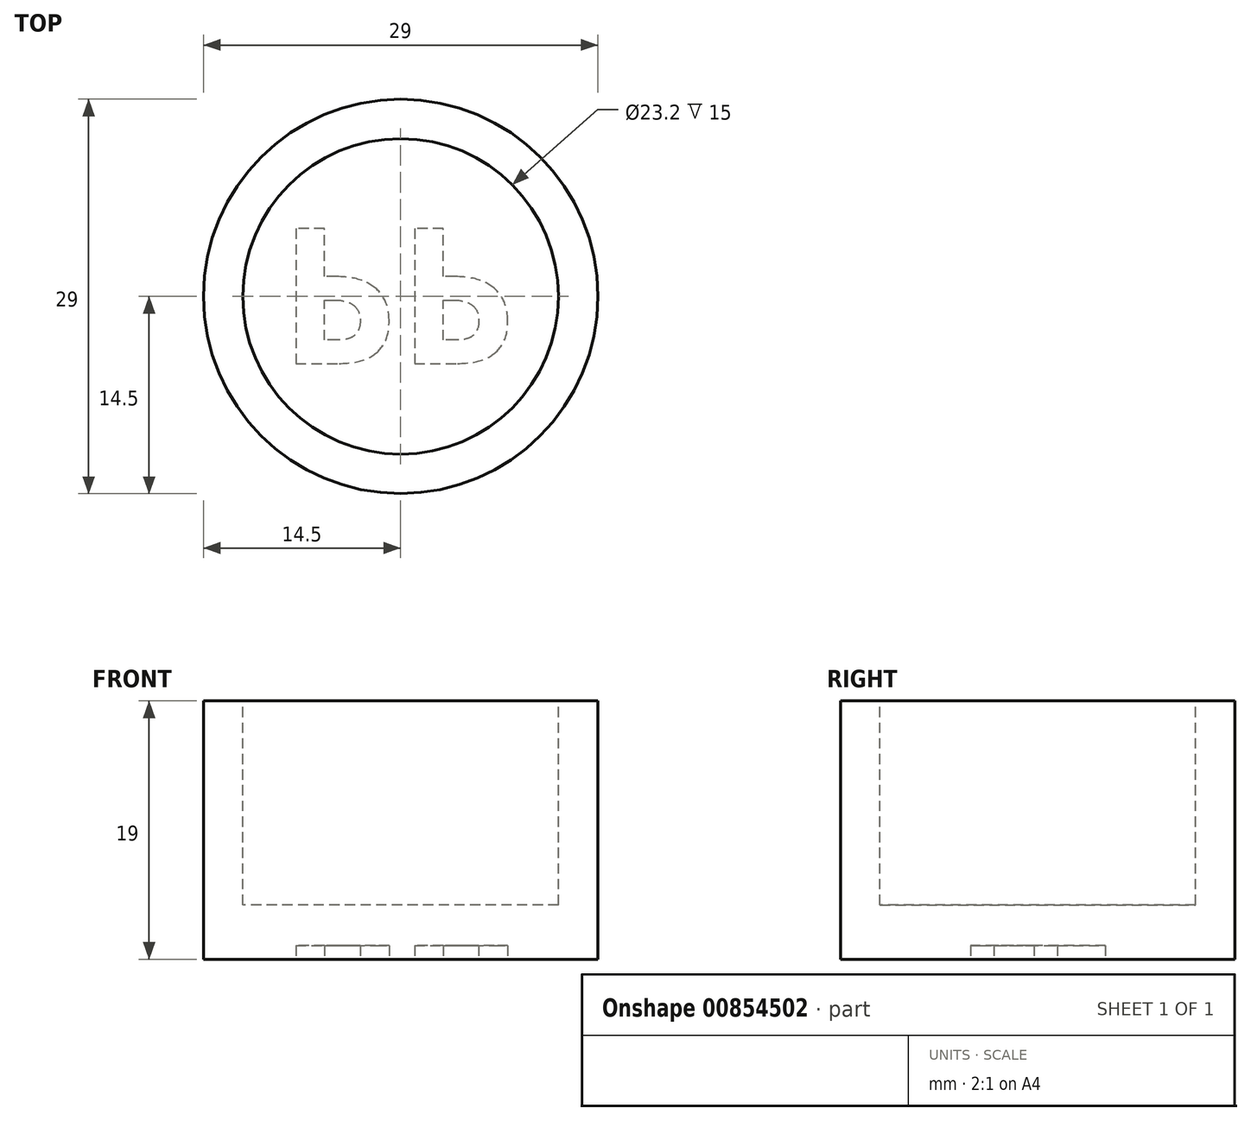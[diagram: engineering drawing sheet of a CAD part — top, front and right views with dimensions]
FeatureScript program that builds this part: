
annotation { "Feature Type Name" : "Feature", "Feature Type Description" : "" }
export const myFeature = defineFeature(function(context is Context, id is Id, definition is map)
    precondition{}
    {
        {
            var Q0;
            Q0=qCreatedBy(makeId("Top.planeOp"),FACE);
            var sketch = newSketch(context, id + "F0", { "sketchPlane" : qUnion([Q0])});
            skCircle(sketch, "E0", {"center": v(0, 0) * mm, "radius": 14.5 * mm});
            skSolve(sketch);
        }
        {
            var Q0;
            Q0 = qSketchRegion(id + "F0", true);
            extrude(context, id + "F1", {"entities" : qUnion([Q0]), "depth" : 19 * mm, "offsetDistance" : 25 * mm});
        }
        {
            var Q0;
            Q0=makeQuery(id+"F1.opExtrude","CAP_FACE",FACE,{"disambiguationData":[OSD([sQuery(id+"F0.wireOp",EDGE,"E0")])],"isStart":false});
            var sketch = newSketch(context, id + "F2", { "sketchPlane" : qUnion([Q0])});
            skCircle(sketch, "E1", {"center": v(0, 0) * mm, "radius": 11.6 * mm});
            skSolve(sketch);
        }
        {
            var Q0;
            Q0 = qSketchRegion(id + "F2", true);
            extrude(context, id + "F3", {"entities" : qUnion([Q0]), "operationType" : NewBodyOperationType.REMOVE, "oppositeDirection" : true, "depth" : 15 * mm, "offsetDistance" : 25 * mm});
        }
        {
            var Q0;
            Q0=makeQuery(id+"F1.opExtrude","CAP_FACE",FACE,{"disambiguationData":[OSD([sQuery(id+"F0.wireOp",EDGE,"E0")])],"isStart":true});
            var sketch = newSketch(context, id + "F4", { "sketchPlane" : qUnion([Q0])});
            skText(sketch, "E2", { "text": "PP", "fontName": "OpenSans-Bold.ttf"});
            const initialGuessF4  = {"E2": [-0.00895, -0.00498, 1, 0, 0.01]};
            skSetInitialGuess(sketch, initialGuessF4);
            skSolve(sketch);
        }
        {
            var Q0;
            Q0 = qSketchRegion(id + "F4", true);
            extrude(context, id + "F5", {"entities" : qUnion([Q0]), "operationType" : NewBodyOperationType.REMOVE, "oppositeDirection" : true, "depth" : 1 * mm, "offsetDistance" : 25 * mm});
        }
    });
